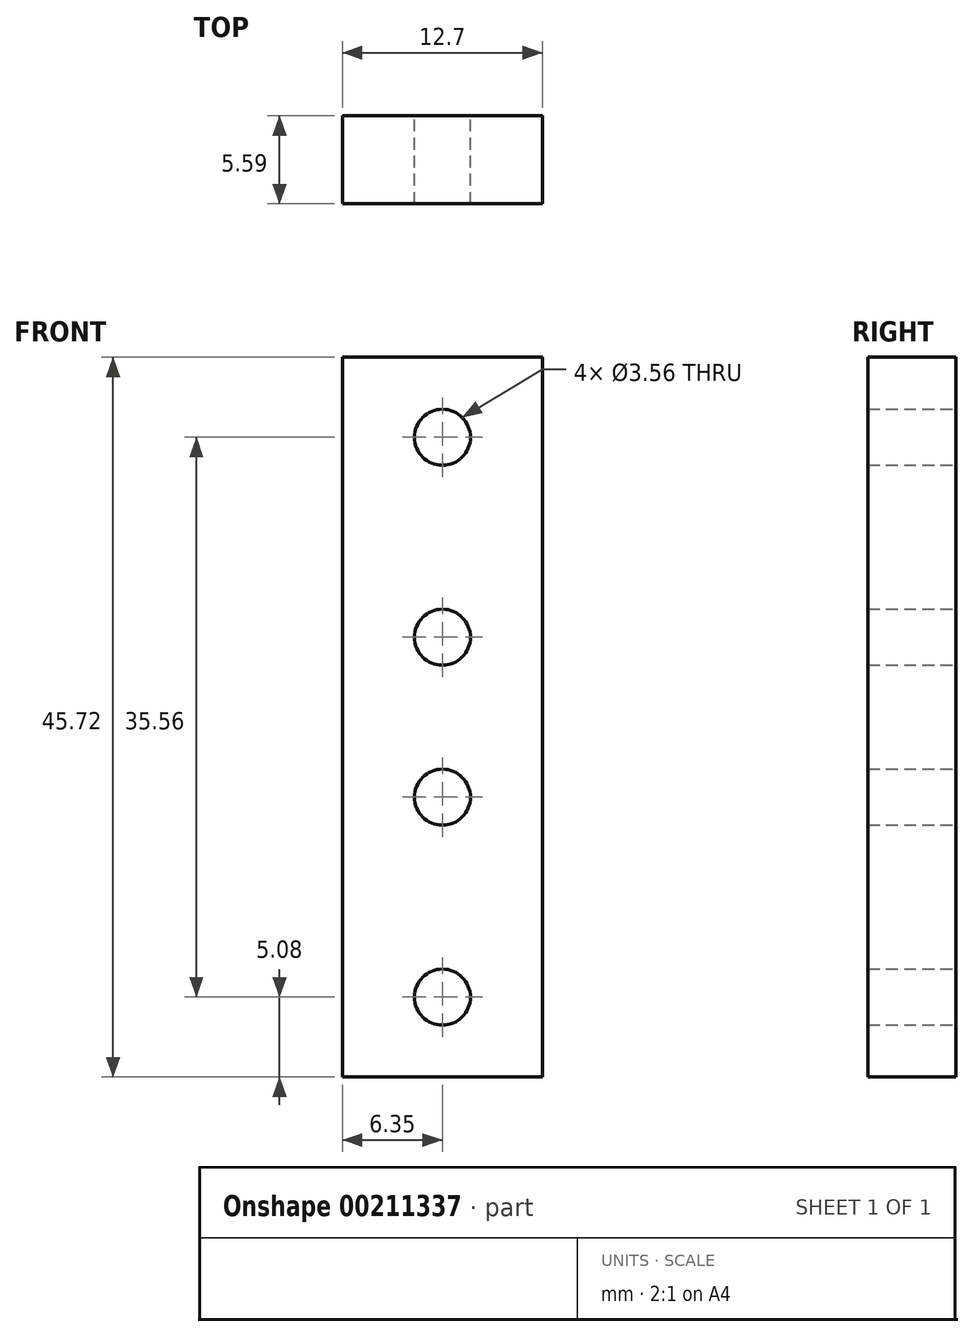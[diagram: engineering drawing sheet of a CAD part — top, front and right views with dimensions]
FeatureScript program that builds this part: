
annotation { "Feature Type Name" : "Feature", "Feature Type Description" : "" }
export const myFeature = defineFeature(function(context is Context, id is Id, definition is map)
    precondition{}
    {
        {
            var Q0;
            Q0=qCreatedBy(makeId("Front.planeOp"),FACE);
            var sketch = newSketch(context, id + "F0", { "sketchPlane" : qUnion([Q0])});
            skLineSegment(sketch, "E0.bottom", {"start": v(0, 0) * mm, "end": v(12.7, 0) * mm});
            skLineSegment(sketch, "E0.top", {"start": v(0, 45.72) * mm, "end": v(12.7, 45.72) * mm});
            skLineSegment(sketch, "E0.left", {"start": v(0, 0) * mm, "end": v(0, 45.72) * mm});
            skLineSegment(sketch, "E0.right", {"start": v(12.7, 0) * mm, "end": v(12.7, 45.72) * mm});
            skCircle(sketch, "E1", {"center": v(6.35, 40.64) * mm, "radius": 1.78 * mm});
            skPoint(sketch, "E1.centerSnap0", {"position": v(6.35, 45.72) * mm});
            skCircle(sketch, "E2", {"center": v(6.35, 27.94) * mm, "radius": 1.78 * mm});
            skLineSegment(sketch, "E3", {"start": v(0, 22.86) * mm, "end": v(12.7, 22.86) * mm, "construction": true});
            skCircle(sketch, "E4.MirrorC", {"center": v(6.35, 5.08) * mm, "radius": 1.78 * mm});
            skCircle(sketch, "E5.MirrorC", {"center": v(6.35, 17.78) * mm, "radius": 1.78 * mm});
            skSolve(sketch);
        }
        {
            var Q0;
            Q0=makeQuery(id+"F0.imprint","IMPRINT",FACE,{"disambiguationData":[TD([[makeQuery(id+"F0.imprint","IMPRINT",EDGE,{"derivedFrom":sQuery(id+"F0.wireOp",EDGE,"E0.bottom")}),1.0]])]});
            extrude(context, id + "F1", {"entities" : qUnion([Q0]), "depth" : 5.6 * mm});
        }
    });
